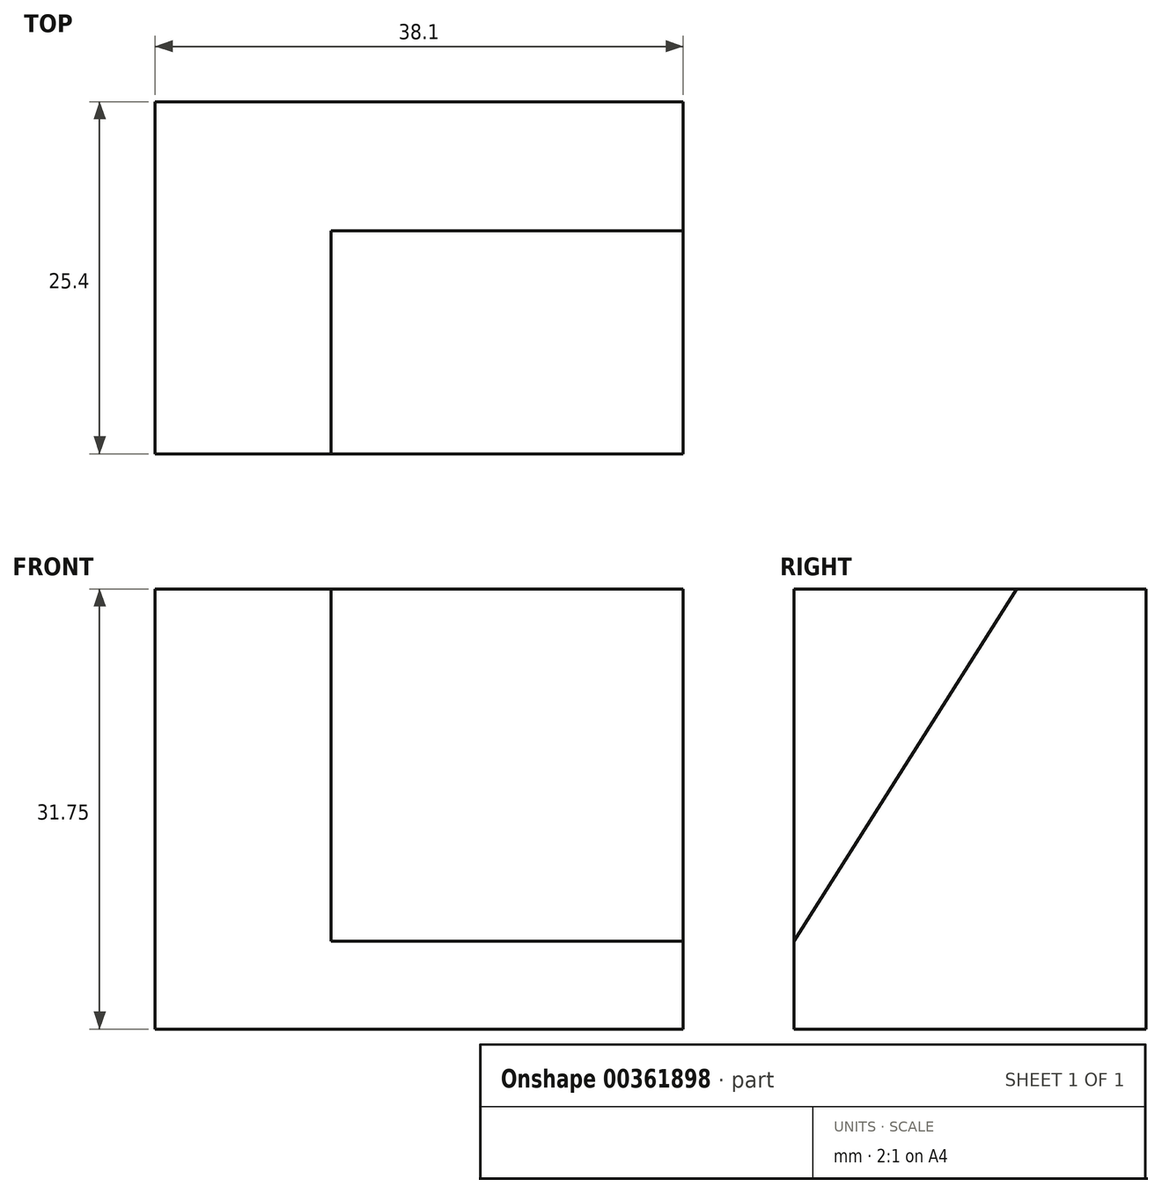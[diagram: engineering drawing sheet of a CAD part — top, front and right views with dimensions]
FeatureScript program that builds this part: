
annotation { "Feature Type Name" : "Feature", "Feature Type Description" : "" }
export const myFeature = defineFeature(function(context is Context, id is Id, definition is map)
    precondition{}
    {
        {
            var Q0;
            Q0=qCreatedBy(makeId("Top.planeOp"),FACE);
            var sketch = newSketch(context, id + "F0", { "sketchPlane" : qUnion([Q0])});
            skLineSegment(sketch, "E0", {"start": v(0, 0) * mm, "end": v(0, 25.4) * mm});
            skLineSegment(sketch, "E1", {"start": v(0, 25.4) * mm, "end": v(38.1, 25.4) * mm});
            skLineSegment(sketch, "E2", {"start": v(38.1, 25.4) * mm, "end": v(38.1, 0) * mm});
            skLineSegment(sketch, "E3", {"start": v(38.1, 0) * mm, "end": v(0, 0) * mm});
            skSolve(sketch);
        }
        {
            var Q0;
            Q0 = qSketchRegion(id + "F0", true);
            extrude(context, id + "F1", {"entities" : qUnion([Q0]), "depth" : 31.75 * mm});
        }
        {
            var Q0;
            Q0=makeQuery(id+"F1.opExtrude","SWEPT_FACE",FACE,{"disambiguationData":[OSD([sQuery(id+"F0.wireOp",EDGE,"E2")])]});
            var sketch = newSketch(context, id + "F2", { "sketchPlane" : qUnion([Q0])});
            skLineSegment(sketch, "E4", {"start": v(16.07, 31.75) * mm, "end": v(0, 6.35) * mm});
            skLineSegment(sketch, "E5", {"start": v(0, 6.35) * mm, "end": v(0, 31.75) * mm});
            skLineSegment(sketch, "E6", {"start": v(0, 31.75) * mm, "end": v(16.07, 31.75) * mm});
            skSolve(sketch);
        }
        {
            var Q0;
            Q0=makeQuery(id+"F2.imprint","IMPRINT",FACE,{"disambiguationData":[TD([[makeQuery(id+"F2.imprint","IMPRINT",EDGE,{"derivedFrom":sQuery(id+"F2.wireOp",EDGE,"E4")}),-1.0]])]});
            extrude(context, id + "F3", {"entities" : qUnion([Q0]), "operationType" : NewBodyOperationType.REMOVE, "oppositeDirection" : true, "depth" : 25.4 * mm});
        }
    });
